# Revit family: Showerhead-American_Standard-Studio_S-1660.528
name_source: partatom
category: Plumbing Fixtures
revit_build: Autodesk Revit 2014 (Build: 20130308_1515(x64)
units: mm (PartAtom-declared; Revit-internal decimal feet)

## types (1)
- 1660.528
    Assembly Code = D2010710
    CW Connection = Yes
    CWFU = 3
    Default Elevation = 0"
    Description = Studio S Water-Saving Showerhead
    Finish = Brass-American Standard-002-Polished Chrome
    Flow Rate = 1.8 gpm / 6.8 L/min.
    HW Connection = Yes
    HWFU = 3
    Installation Type = Wall Mounted
    Length = 8"
    Manufacturer = American Standard
    Material = Brass-American Standard-002-Polished Chrome
    Model = 1660.528
    Price = Prices may vary. Please consult Manufacturer Representative for most up-to-date price list.
    Product Documentation Link = https://www.americanstandard-us.com
    Product Page URL = https://www.americanstandard-us.com
    Specification = Showerhead shall save 30% in water usage. Showerhead shall have 1 spray pattern and brass ball joint. Fitting shall be American Standard Model 1660.528.
    URL = https://www.americanstandard-us.com
    Vent Connection = No
    WFU = 4
    Warranty Information = One Year General Product Warranty
    Waste Connection = Yes
    Water Connection Diameter = 1/2"

## geometry (parser evidence)
native form markers: Sweep x1
no freeform markers — native parametric forms only
